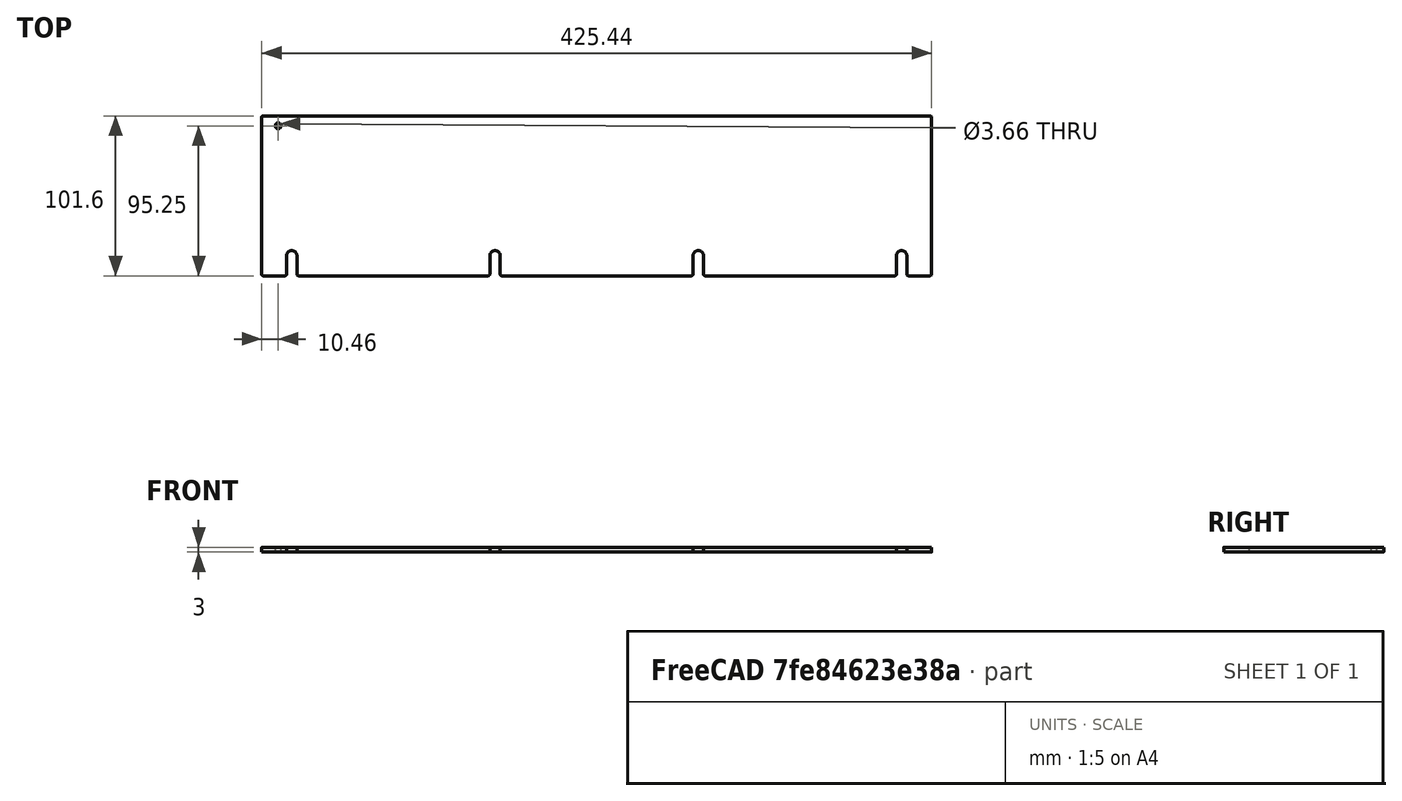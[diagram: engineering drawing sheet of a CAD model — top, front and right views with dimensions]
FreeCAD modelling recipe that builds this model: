
FCSTD DOCUMENT  (FreeCAD 0.21R33675 (Git))
Label: plain_wall_16p75in
License: All rights reserved
LicenseURL: http://en.wikipedia.org/wiki/All_rights_reserved
objects: Sketcher::SketchObject×1, Spreadsheet::Sheet×1, PartDesign::Pad×1, PartDesign::Body×1
note: 4 computed .brp shape members not serialized (recipe doc carries the construction recipe); baked Part::Feature solids carry a one-line shape summary decoded from their .brp

FEATURE [Sketcher::SketchObject] Sketch
  FullyConstrained = true
  MapMode = 5
  Support = -> [XY_Plane]
  expr: Constraints[125] = Spreadsheet.BracketHoleFromSide
  expr: Constraints[126] = Spreadsheet.UpperBracketHoleFromTop
  expr: Constraints[127] = Spreadsheet.BracketHoleDiameter
  expr: Constraints[19] = Spreadsheet.FilletRadius
  expr: Constraints[21] = Spreadsheet.Height
  expr: Constraints[22] = Spreadsheet.Length
  expr: Constraints[27] = Spreadsheet.MountHoleDistanceFromBottom
  expr: Constraints[29] = Spreadsheet.MountHoleDiameter
  expr: Constraints[49] = Spreadsheet.MountHoleSideMargin
  expr: Constraints[53] = Spreadsheet.MountHoleDistanceFromBottom
  sketch-geometry (49):
    g0: ArcOfCircle CenterX=-211.725 CenterY=49.8 CenterZ=0 NormalX=0 NormalY=0 NormalZ=1 AngleXU=0 Radius=1 StartAngle=1.5708 EndAngle=3.14159
    g1: LineSegment StartX=-211.725 StartY=50.8 StartZ=0 EndX=211.725 EndY=50.8 EndZ=0
    g2: ArcOfCircle CenterX=211.725 CenterY=49.8 CenterZ=0 NormalX=0 NormalY=0 NormalZ=1 AngleXU=0 Radius=1 StartAngle=1e-16 EndAngle=1.5708
    g3: LineSegment StartX=212.725 StartY=49.8 StartZ=0 EndX=212.725 EndY=-49.8 EndZ=0
    g4: ArcOfCircle CenterX=211.725 CenterY=-49.8 CenterZ=0 NormalX=0 NormalY=0 NormalZ=1 AngleXU=0 Radius=1 StartAngle=4.71239 EndAngle=6.28319
    g5: LineSegment StartX=211.725 StartY=-50.8 StartZ=0 EndX=-211.725 EndY=-50.8 EndZ=0
    g6: ArcOfCircle CenterX=-211.725 CenterY=-49.8 CenterZ=0 NormalX=0 NormalY=0 NormalZ=1 AngleXU=0 Radius=1 StartAngle=3.14159 EndAngle=4.71239
    g7: LineSegment StartX=-212.725 StartY=-49.8 StartZ=0 EndX=-212.725 EndY=49.8 EndZ=0
    g8: GeomPoint X=-212.725 Y=50.8 Z=0
    g9: GeomPoint X=212.725 Y=-50.8 Z=0
    g10: LineSegment StartX=-64.5583 StartY=-38.1 StartZ=0 EndX=64.5583 EndY=-38.1 EndZ=0
    g11: LineSegment StartX=0 StartY=-50.8 StartZ=0 EndX=0 EndY=-38.1 EndZ=0
    g12: Circle CenterX=-64.5583 CenterY=-38.1 CenterZ=0 NormalX=0 NormalY=0 NormalZ=1 AngleXU=0 Radius=3.302
    g13: Circle CenterX=64.5583 CenterY=-38.1 CenterZ=0 NormalX=0 NormalY=0 NormalZ=1 AngleXU=0 Radius=3.302
    g14: LineSegment StartX=-64.5583 StartY=-38.1 StartZ=0 EndX=-193.675 EndY=-38.1 EndZ=0
    g15: LineSegment StartX=-193.675 StartY=-38.1 StartZ=0 EndX=-212.725 EndY=-38.1 EndZ=0
    g16: LineSegment StartX=64.5583 StartY=-38.1 StartZ=0 EndX=193.675 EndY=-38.1 EndZ=0
    g17: LineSegment StartX=193.675 StartY=-38.1 StartZ=0 EndX=212.725 EndY=-38.1 EndZ=0
    g18: Circle CenterX=-193.675 CenterY=-38.1 CenterZ=0 NormalX=0 NormalY=0 NormalZ=1 AngleXU=0 Radius=3.302
    g19: Circle CenterX=193.675 CenterY=-38.1 CenterZ=0 NormalX=0 NormalY=0 NormalZ=1 AngleXU=0 Radius=3.302
    g20: LineSegment StartX=0 StartY=-38.1 StartZ=0 EndX=0 EndY=-50.8 EndZ=0
    g21: ArcOfCircle CenterX=-193.675 CenterY=-38.1 CenterZ=0 NormalX=0 NormalY=0 NormalZ=1 AngleXU=0 Radius=3.302 StartAngle=2e-16 EndAngle=3.14159
    g22: LineSegment StartX=-196.977 StartY=-38.1 StartZ=0 EndX=-196.977 EndY=-49.8 EndZ=0
    g23: LineSegment StartX=-190.373 StartY=-38.1 StartZ=0 EndX=-190.373 EndY=-49.8 EndZ=0
    g24: ArcOfCircle CenterX=-197.977 CenterY=-49.8 CenterZ=0 NormalX=0 NormalY=0 NormalZ=1 AngleXU=0 Radius=1 StartAngle=4.71239 EndAngle=6.28319
    g25: ArcOfCircle CenterX=-189.373 CenterY=-49.8 CenterZ=0 NormalX=0 NormalY=0 NormalZ=1 AngleXU=0 Radius=1 StartAngle=3.14159 EndAngle=4.71239
    g26: ArcOfCircle CenterX=-64.5583 CenterY=-38.1 CenterZ=0 NormalX=0 NormalY=0 NormalZ=1 AngleXU=0 Radius=3.302 StartAngle=2e-15 EndAngle=3.14159
    g27: LineSegment StartX=-67.8603 StartY=-38.1 StartZ=0 EndX=-67.8603 EndY=-49.8 EndZ=0
    g28: LineSegment StartX=-61.2563 StartY=-38.1 StartZ=0 EndX=-61.2563 EndY=-49.8 EndZ=0
    g29: ArcOfCircle CenterX=-68.8603 CenterY=-49.8 CenterZ=0 NormalX=0 NormalY=0 NormalZ=1 AngleXU=0 Radius=1 StartAngle=4.71239 EndAngle=6.28319
    g30: ArcOfCircle CenterX=-60.2563 CenterY=-49.8 CenterZ=0 NormalX=0 NormalY=0 NormalZ=1 AngleXU=0 Radius=1 StartAngle=3.14159 EndAngle=4.71239
    g31: ArcOfCircle CenterX=64.5583 CenterY=-38.1 CenterZ=0 NormalX=0 NormalY=0 NormalZ=1 AngleXU=0 Radius=3.302 StartAngle=9e-16 EndAngle=3.14159
    g32: LineSegment StartX=61.2563 StartY=-38.1 StartZ=0 EndX=61.2563 EndY=-49.8 EndZ=0
    g33: LineSegment StartX=67.8603 StartY=-38.1 StartZ=0 EndX=67.8603 EndY=-49.8 EndZ=0
    g34: ArcOfCircle CenterX=60.2563 CenterY=-49.8 CenterZ=0 NormalX=0 NormalY=0 NormalZ=1 AngleXU=0 Radius=1 StartAngle=4.71239 EndAngle=6.28319
    g35: ArcOfCircle CenterX=68.8603 CenterY=-49.8 CenterZ=0 NormalX=0 NormalY=0 NormalZ=1 AngleXU=0 Radius=1 StartAngle=3.14159 EndAngle=4.71239
    g36: ArcOfCircle CenterX=193.675 CenterY=-38.1 CenterZ=0 NormalX=0 NormalY=0 NormalZ=1 AngleXU=0 Radius=3.302 StartAngle=-1.07e-14 EndAngle=3.14159
    g37: LineSegment StartX=190.373 StartY=-38.1 StartZ=0 EndX=190.373 EndY=-49.8 EndZ=0
    g38: LineSegment StartX=196.977 StartY=-38.1 StartZ=0 EndX=196.977 EndY=-49.8 EndZ=0
    g39: ArcOfCircle CenterX=189.373 CenterY=-49.8 CenterZ=0 NormalX=0 NormalY=0 NormalZ=1 AngleXU=0 Radius=1 StartAngle=4.71239 EndAngle=6.28319
    g40: ArcOfCircle CenterX=197.977 CenterY=-49.8 CenterZ=0 NormalX=0 NormalY=0 NormalZ=1 AngleXU=0 Radius=1 StartAngle=3.14159 EndAngle=4.71239
    g41: LineSegment StartX=-211.725 StartY=-50.8 StartZ=0 EndX=-197.977 EndY=-50.8 EndZ=0
    g42: LineSegment StartX=-189.373 StartY=-50.8 StartZ=0 EndX=-68.8603 EndY=-50.8 EndZ=0
    g43: LineSegment StartX=-60.2563 StartY=-50.8 StartZ=0 EndX=60.2563 EndY=-50.8 EndZ=0
    g44: LineSegment StartX=68.8603 StartY=-50.8 StartZ=0 EndX=189.373 EndY=-50.8 EndZ=0
    g45: LineSegment StartX=197.977 StartY=-50.8 StartZ=0 EndX=211.725 EndY=-50.8 EndZ=0
    g46: LineSegment StartX=-212.725 StartY=50.8 StartZ=0 EndX=-202.26 EndY=50.8 EndZ=0
    g47: LineSegment StartX=-202.26 StartY=50.8 StartZ=0 EndX=-202.26 EndY=44.45 EndZ=0
    g48: Circle CenterX=-202.26 CenterY=44.45 CenterZ=0 NormalX=0 NormalY=0 NormalZ=1 AngleXU=0 Radius=1.8288
  constraints (128):
    c: Tangent(g0,g1) = 1.5708
    c: Tangent(g1,g2) = 1.5708
    c: Tangent(g2,g3) = 1.5708
    c: Tangent(g3,g4) = 1.5708
    c: Tangent(g4,g5) = 1.5708
    c: Tangent(g5,g6) = 1.5708
    c: Tangent(g6,g7) = 1.5708
    c: Tangent(g7,g0) = 1.5708
    c: Horizontal(g1)
    c: Horizontal(g5)
    c: Vertical(g3)
    c: Vertical(g7)
    c: Equal(g0,g2)
    c: Equal(g2,g4)
    c: Equal(g4,g6)
    c: PointOnObject(g8,g1)
    c: PointOnObject(g8,g7)
    c: PointOnObject(g9,g3)
    c: PointOnObject(g9,g5)
    c: Radius(g2) = 1
    c: Symmetric(g8,g9,g-1)
    c: DistanceY(g4,g1) = 101.6
    c: DistanceX(g0,g2) = 425.45
    c: Horizontal(g10)
    c: Vertical(g11)
    c: PointOnObject(g11,g5)
    c: PointOnObject(g11,g-2)
    c: DistanceY(g11,g11) = 12.7
    c: Coincident(g13,g10)
    c: Diameter(g13) = 6.604
    c: Equal(g12,g13)
    c: Coincident(g12,g10)
    c: Coincident(g14,g12)
    c: Horizontal(g14)
    c: Coincident(g15,g14)
    c: PointOnObject(g15,g7)
    c: Horizontal(g15)
    c: Coincident(g16,g13)
    c: Horizontal(g16)
    c: Coincident(g17,g16)
    c: PointOnObject(g17,g3)
    c: Horizontal(g17)
    c: Equal(g17,g15)
    c: Equal(g14,g10)
    c: Equal(g10,g16)
    c: Coincident(g18,g14)
    c: Coincident(g19,g16)
    c: Equal(g18,g12)
    c: Equal(g13,g19)
    c: DistanceX(g15,g15) = 19.05
    c: PointOnObject(g20,g10)
    c: Vertical(g20)
    c: Coincident(g20,g11)
    c: DistanceY(g20,g20) = 12.7
    c: Coincident(g21,g14)
    c: PointOnObject(g21,g15)
    c: PointOnObject(g21,g14)
    c: PointOnObject(g21,g18)
    c: Coincident(g22,g21)
    c: Vertical(g22)
    c: Coincident(g23,g21)
    c: Vertical(g23)
    c: Equal(g22,g23)
    c: Tangent(g24,g22) = 1.5708
    c: Tangent(g24,g5) = 1.5708
    c: Tangent(g25,g23) = -1.5708
    c: Tangent(g25,g5) = 1.5708
    c: Equal(g24,g6)
    c: Coincident(g26,g10)
    c: PointOnObject(g26,g14)
    c: PointOnObject(g26,g10)
    c: PointOnObject(g26,g12)
    c: Coincident(g27,g26)
    c: Vertical(g27)
    c: Coincident(g28,g26)
    c: Vertical(g28)
    c: Equal(g27,g28)
    c: Tangent(g29,g27) = 1.5708
    c: Tangent(g29,g5) = 1.5708
    c: Tangent(g30,g28) = -1.5708
    c: Tangent(g30,g5) = 1.5708
    c: Equal(g29,g6)
    c: Coincident(g31,g10)
    c: PointOnObject(g31,g10)
    c: PointOnObject(g31,g16)
    c: PointOnObject(g31,g13)
    c: Coincident(g32,g31)
    c: Vertical(g32)
    c: Coincident(g33,g31)
    c: Vertical(g33)
    c: Equal(g32,g33)
    c: Tangent(g34,g32) = 1.5708
    c: Tangent(g34,g5) = 1.5708
    c: Tangent(g35,g33) = -1.5708
    c: Tangent(g35,g5) = 1.5708
    c: Equal(g30,g34)
    c: Coincident(g36,g16)
    c: PointOnObject(g36,g16)
    c: PointOnObject(g36,g17)
    c: PointOnObject(g36,g19)
    c: Coincident(g37,g36)
    c: Vertical(g37)
    c: Coincident(g38,g36)
    c: Vertical(g38)
    c: Equal(g37,g38)
    c: Tangent(g40,g38) = -1.5708
    c: Tangent(g39,g37) = 1.5708
    c: Tangent(g39,g5) = 1.5708
    c: Tangent(g40,g5) = 1.5708
    c: Equal(g40,g4)
    c: Coincident(g41,g6)
    c: Coincident(g41,g24)
    c: Coincident(g42,g25)
    c: Coincident(g42,g29)
    c: Coincident(g43,g30)
    c: Coincident(g43,g34)
    c: Coincident(g44,g35)
    c: Coincident(g44,g39)
    c: Coincident(g45,g40)
    c: Coincident(g45,g4)
    c: Horizontal(g46)
    c: Coincident(g8,g46)
    c: Vertical(g47)
    c: Coincident(g46,g47)
    c: Coincident(g48,g47)
    c: DistanceX(g46,g46) = 10.4648
    c: DistanceY(g47,g47) = 6.35
    c: Diameter(g48) = 3.6576
FEATURE [Spreadsheet::Sheet] Spreadsheet
  cells = A2='Parameters; A3='Height; B3(Height)==4 in; A4='Length; B4(Length)==16.75 in; A5='Thickness; B5(Thickness)==3 mm; A6='FilletRadius; B6(FilletRadius)==1 mm; A7='MountHoleDiameter; B7(MountHoleDiameter)==0.26 in; A8='MountHoleDistanceFromBottom; B8(MountHoleDistanceFromBottom)==0.5 in; A9='MountHoleSideMargin; B9(MountHoleSideMargin)==0.75 in; A11='BracketWidth; B11(BracketWidth)==0.5 in; A12='BracketHoleDiameter; B12(BracketHoleDiameter)==0.144 in; A13='BracketHoleOffset; B13(BracketHoleOffset)==0.412 in; A14='UpperBracketHoleFromTop; B14(UpperBracketHoleFromTop)==0.5 * BracketWidth; A15='BracketHoleFromSide; B15(BracketHoleFromSide)==BracketHoleOffset
FEATURE [PartDesign::Pad] Pad
  Direction = (0,0,1)
  Length = 3
  Length2 = 10
  Profile = -> Sketch
  ReferenceAxis = -> Sketch [N_Axis]
  Type = 0
  expr: Length = Spreadsheet.Thickness
FEATURE [PartDesign::Body] Body
  Group = -> [Sketch,Pad]
  Origin = -> Origin
  Tip = -> Pad
